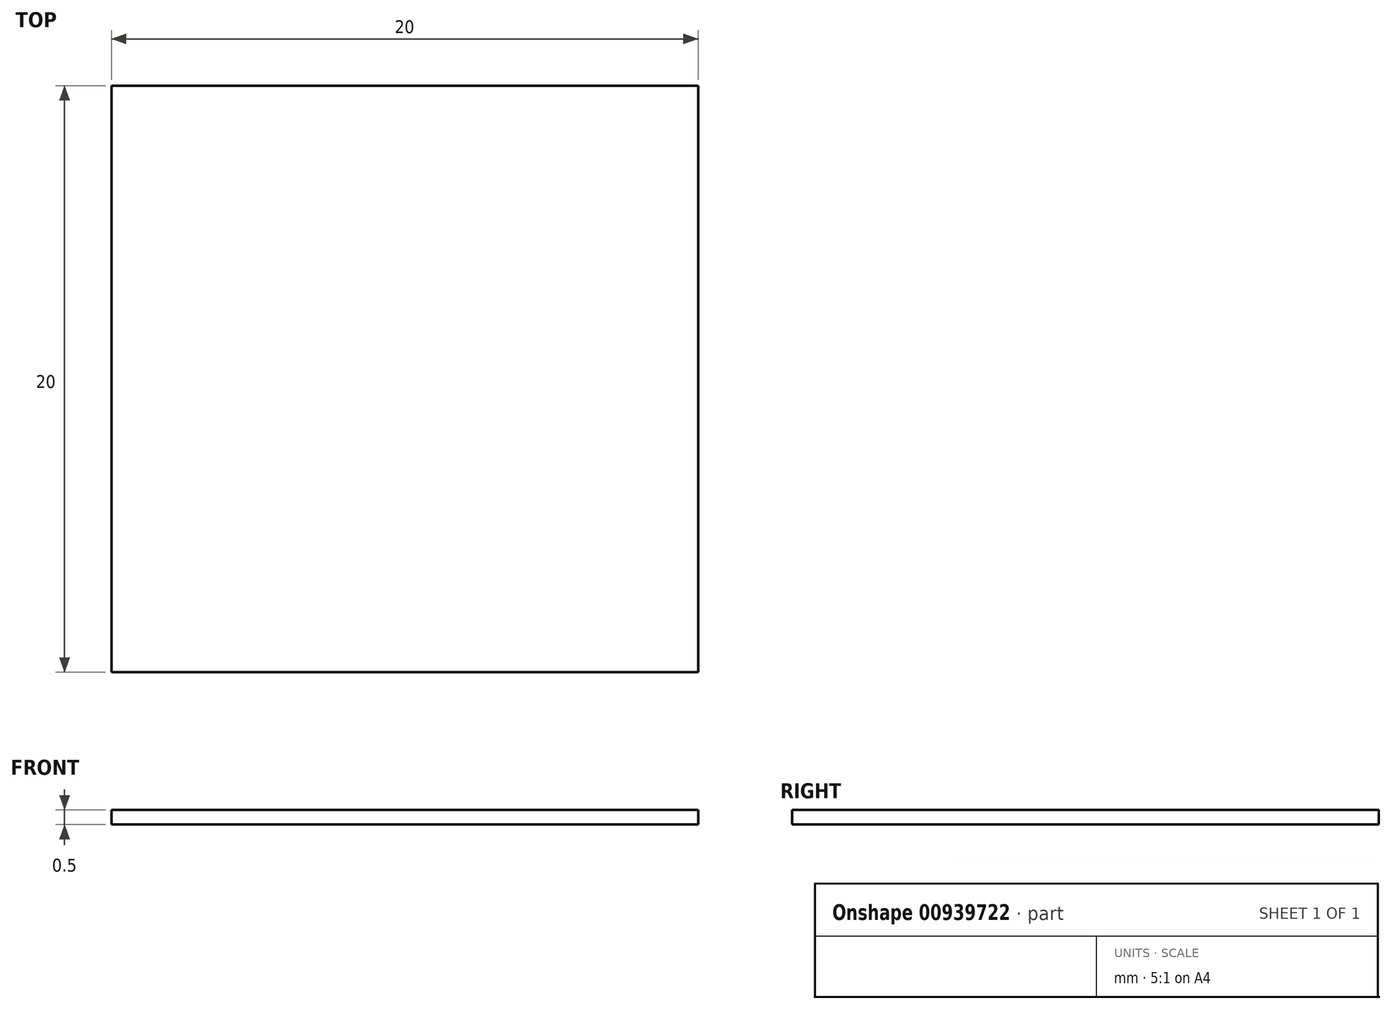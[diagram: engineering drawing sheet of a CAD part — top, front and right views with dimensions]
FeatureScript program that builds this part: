
annotation { "Feature Type Name" : "Feature", "Feature Type Description" : "" }
export const myFeature = defineFeature(function(context is Context, id is Id, definition is map)
    precondition{}
    {
        {
            var Q0;
            Q0=qCreatedBy(makeId("Top.planeOp"),FACE);
            var sketch = newSketch(context, id + "F0", { "sketchPlane" : qUnion([Q0])});
            skLineSegment(sketch, "E0.bottom", {"start": v(10, 10) * mm, "end": v(-10, 10) * mm});
            skLineSegment(sketch, "E0.top", {"start": v(10, -10) * mm, "end": v(-10, -10) * mm});
            skLineSegment(sketch, "E0.left", {"start": v(10, 10) * mm, "end": v(10, -10) * mm});
            skLineSegment(sketch, "E0.right", {"start": v(-10, 10) * mm, "end": v(-10, -10) * mm});
            skPoint(sketch, "E0.middle", {"position": v(0, 0) * mm});
            skSolve(sketch);
        }
        {
            var Q0;
            Q0=qSketchRegion(id+"F0",true);
            extrude(context, id + "F1", {"entities" : qUnion([Q0]), "depth" : 0.5 * mm, "offsetDistance" : 25 * mm});
        }
    });
